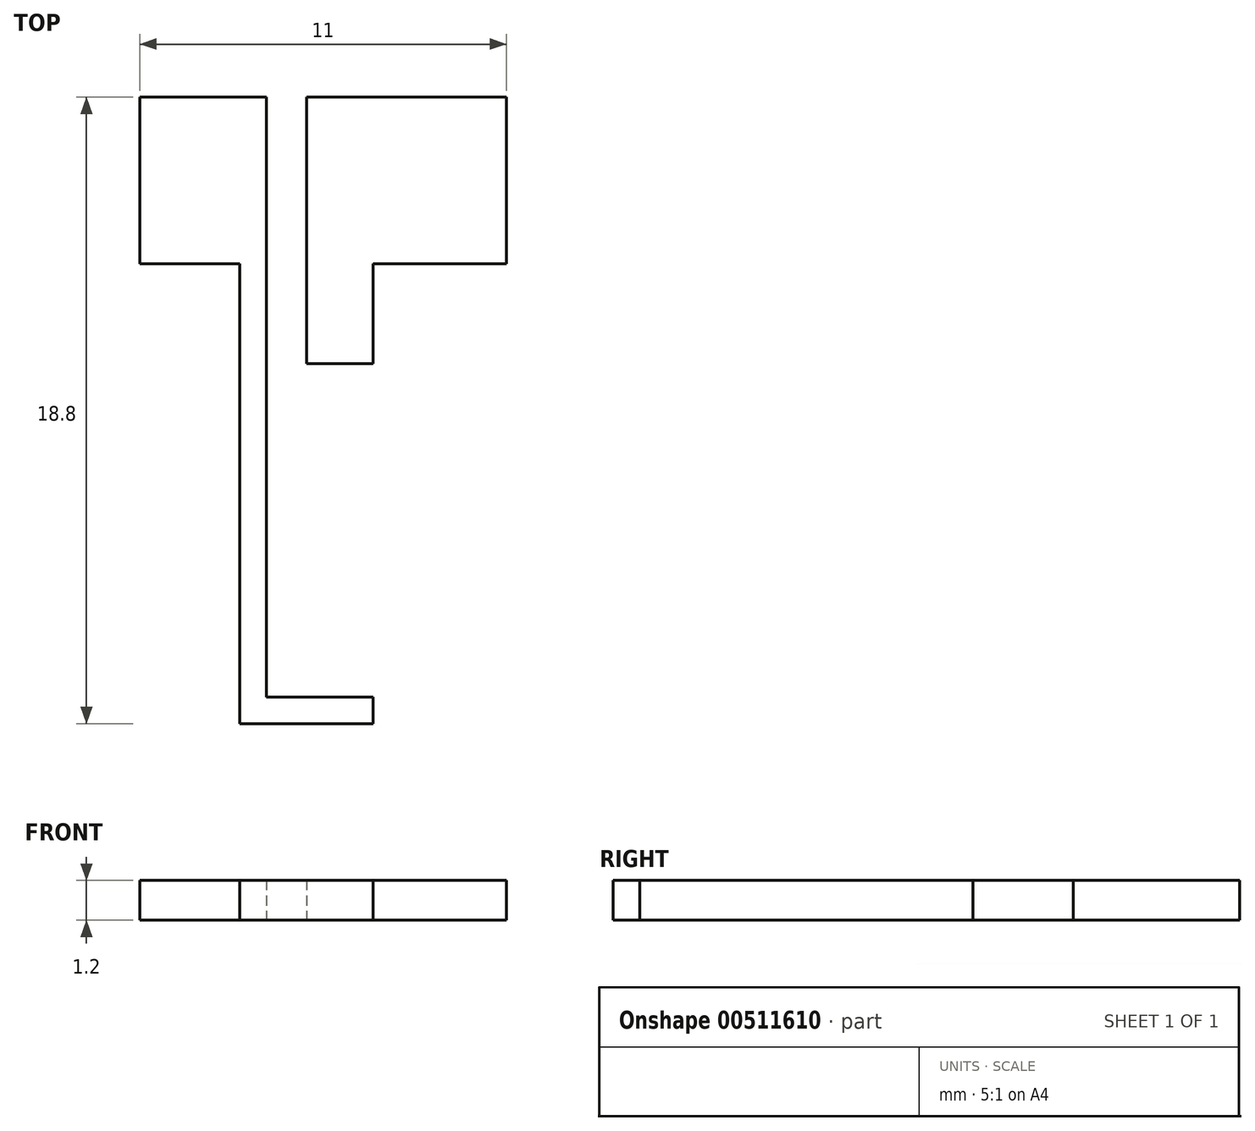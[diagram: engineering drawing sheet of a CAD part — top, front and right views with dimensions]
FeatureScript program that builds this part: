
annotation { "Feature Type Name" : "Feature", "Feature Type Description" : "" }
export const myFeature = defineFeature(function(context is Context, id is Id, definition is map)
    precondition{}
    {
        {
            var Q0;
            Q0=qCreatedBy(makeId("Top.planeOp"),FACE);
            var sketch = newSketch(context, id + "F0", { "sketchPlane" : qUnion([Q0])});
            skLineSegment(sketch, "E0.bottom", {"start": v(1, 2.5) * mm, "end": v(-1, 2.5) * mm});
            skLineSegment(sketch, "E0.top", {"start": v(1, -2.5) * mm, "end": v(-1, -2.5) * mm});
            skLineSegment(sketch, "E0.left", {"start": v(1, 2.5) * mm, "end": v(1, -2.5) * mm});
            skLineSegment(sketch, "E0.right", {"start": v(-1, 2.5) * mm, "end": v(-1, -2.5) * mm});
            skPoint(sketch, "E0.middle", {"position": v(0, 0) * mm});
            skLineSegment(sketch, "E1.bottom", {"start": v(-1, 2.5) * mm, "end": v(1, 2.5) * mm});
            skLineSegment(sketch, "E1.top", {"start": v(-1, 2.5) * mm, "end": v(1, 2.5) * mm});
            skLineSegment(sketch, "E1.left", {"start": v(-1, 2.5) * mm, "end": v(-1, 2.5) * mm});
            skLineSegment(sketch, "E1.right", {"start": v(1, 2.5) * mm, "end": v(1, 2.5) * mm});
            skLineSegment(sketch, "E2.top", {"start": v(-1, 15.5) * mm, "end": v(1, 15.5) * mm});
            skLineSegment(sketch, "E2.left", {"start": v(-1, 2.5) * mm, "end": v(-1, 12.5) * mm});
            skLineSegment(sketch, "E2.right", {"start": v(1, 2.5) * mm, "end": v(1, 14.39) * mm});
            skLineSegment(sketch, "E3.bottom", {"start": v(1, -2.5) * mm, "end": v(-3, -2.5) * mm});
            skLineSegment(sketch, "E3.top", {"start": v(1, -3.3) * mm, "end": v(-3, -3.3) * mm});
            skLineSegment(sketch, "E3.left", {"start": v(1, -2.5) * mm, "end": v(1, -3.3) * mm});
            skLineSegment(sketch, "E3.right", {"start": v(-3, -2.5) * mm, "end": v(-3, -3.3) * mm});
            skLineSegment(sketch, "E4.bottom", {"start": v(-3, -2.5) * mm, "end": v(-2.2, -2.5) * mm});
            skLineSegment(sketch, "E4.top", {"start": v(-3, 15.5) * mm, "end": v(-2.2, 15.5) * mm});
            skLineSegment(sketch, "E4.left", {"start": v(-3, -2.5) * mm, "end": v(-3, 12.5) * mm});
            skLineSegment(sketch, "E4.right", {"start": v(-2.2, -2.5) * mm, "end": v(-2.2, 12.5) * mm});
            skLineSegment(sketch, "E5.bottom", {"start": v(-3, 15.5) * mm, "end": v(-6, 15.5) * mm});
            skLineSegment(sketch, "E5.top", {"start": v(-3, 10.5) * mm, "end": v(-6, 10.5) * mm});
            skLineSegment(sketch, "E5.left", {"start": v(-3, 12.5) * mm, "end": v(-3, 10.5) * mm});
            skLineSegment(sketch, "E5.right", {"start": v(-6, 12.5) * mm, "end": v(-6, 10.5) * mm});
            skLineSegment(sketch, "E6.bottom", {"start": v(0, 15.5) * mm, "end": v(5, 15.5) * mm});
            skLineSegment(sketch, "E6.top", {"start": v(0, 10.5) * mm, "end": v(5, 10.5) * mm});
            skLineSegment(sketch, "E6.left", {"start": v(0, 12.5) * mm, "end": v(0, 10.5) * mm});
            skLineSegment(sketch, "E6.right", {"start": v(5, 12.5) * mm, "end": v(5, 10.5) * mm});
            skLineSegment(sketch, "E7", {"start": v(-6, 10.5) * mm, "end": v(-6, 12.5) * mm});
            skLineSegment(sketch, "E8", {"start": v(5, 10.5) * mm, "end": v(5, 12.5) * mm});
            skLineSegment(sketch, "E9", {"start": v(5, 12.5) * mm, "end": v(5, 15.5) * mm});
            skLineSegment(sketch, "E10", {"start": v(-1, 12.5) * mm, "end": v(-1, 15.5) * mm});
            skLineSegment(sketch, "E11", {"start": v(-2.2, 12.5) * mm, "end": v(-2.2, 15.5) * mm});
            skLineSegment(sketch, "E12", {"start": v(-6, 15.5) * mm, "end": v(-6, 12.5) * mm});
            skLineSegment(sketch, "E13", {"start": v(1, 2.5) * mm, "end": v(1, 7.5) * mm});
            skLineSegment(sketch, "E14", {"start": v(1, 7.5) * mm, "end": v(-1, 7.5) * mm});
            skLineSegment(sketch, "E15", {"start": v(-1, 7.5) * mm, "end": v(-1, 2.5) * mm});
            skSolve(sketch);
        }
        {
            var Q0;
            Q0=makeQuery(id+"F0.imprint","IMPRINT",FACE,{"disambiguationData":[TD([[makeQuery(id+"F0.imprint","IMPRINT",EDGE,{"derivedFrom":sQuery(id+"F0.wireOp",EDGE,"E5.bottom")}),1.0]])]});
            var Q1;
            Q1=makeQuery(id+"F0.imprint","IMPRINT",FACE,{"disambiguationData":[TD([[makeQuery(id+"F0.imprint","IMPRINT",EDGE,{"derivedFrom":sQuery(id+"F0.wireOp",EDGE,"E4.bottom")}),1.0]])]});
            var Q2;
            Q2=makeQuery(id+"F0.imprint","IMPRINT",FACE,{"disambiguationData":[TD([[makeQuery(id+"F0.imprint","IMPRINT",EDGE,{"derivedFrom":sQuery(id+"F0.wireOp",EDGE,"E3.top")}),-1.0]])]});
            var Q3;
            {var subQ5=sQuery(id+"F0.wireOp",EDGE,"E6.right");Q3=makeQuery(id+"F0.imprint","IMPRINT",FACE,{"disambiguationData":[TD([[makeQuery(id+"F0.imprint","IMPRINT",EDGE,{"derivedFrom":subQ5}),-1.0]])]});}
            var Q4;
            {var subQ5=sQuery(id+"F0.wireOp",EDGE,"E6.left");Q4=makeQuery(id+"F0.imprint","IMPRINT",FACE,{"disambiguationData":[TD([[makeQuery(id+"F0.imprint","IMPRINT",EDGE,{"derivedFrom":subQ5}),1.0]])]});}
            var Q5;
            {var subQ1=sQuery(id+"F0.wireOp",EDGE,"E2.top");Q5=makeQuery(id+"F0.imprint","IMPRINT",FACE,{"disambiguationData":[TD([[makeQuery(id+"F0.imprint","IMPRINT",EDGE,{"derivedFrom":subQ1}),-1.0]])]});}
            extrude(context, id + "F1", {"entities" : qUnion([Q0, Q1, Q2, Q3, Q4, Q5]), "depth" : 1.2 * mm, "offsetDistance" : 25 * mm});
        }
    });
